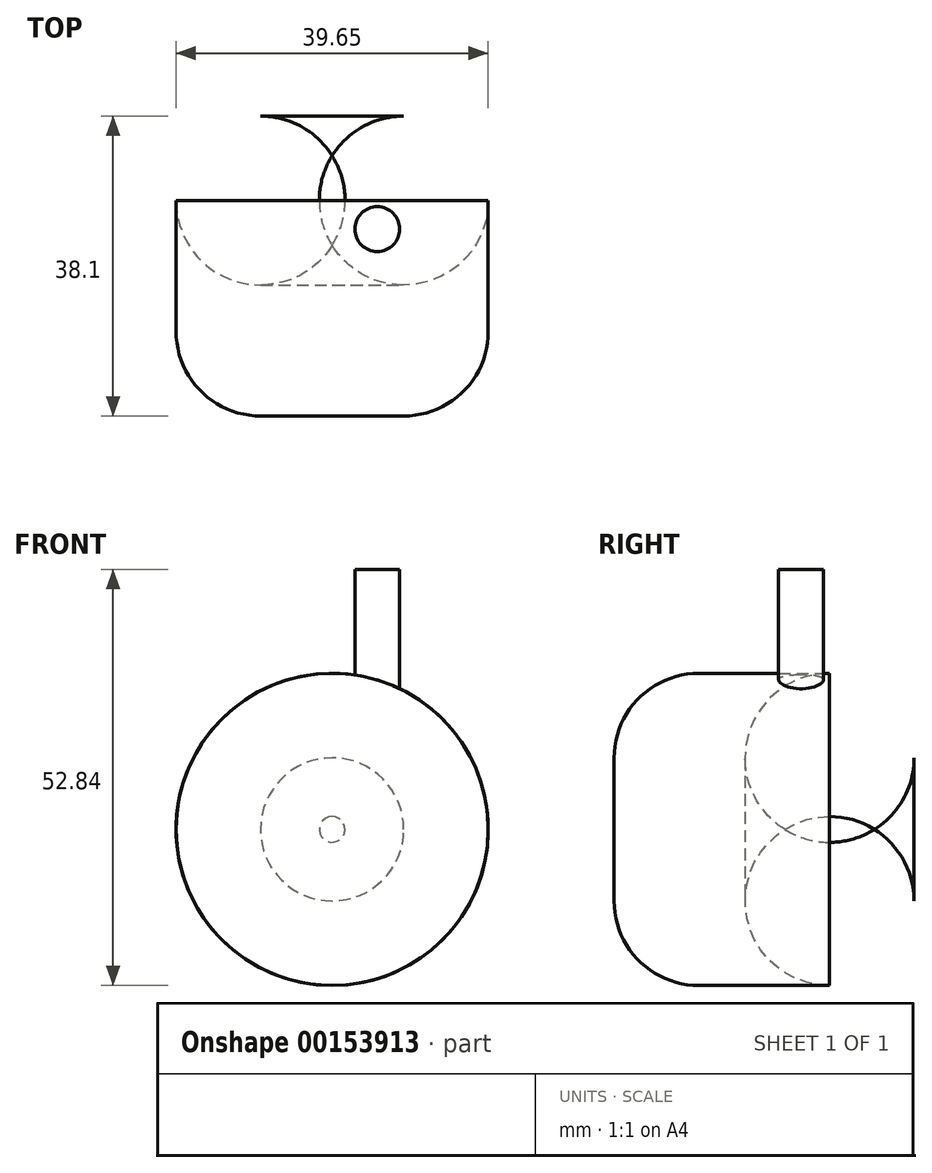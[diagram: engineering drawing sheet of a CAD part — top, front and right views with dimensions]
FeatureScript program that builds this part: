
annotation { "Feature Type Name" : "Feature", "Feature Type Description" : "" }
export const myFeature = defineFeature(function(context is Context, id is Id, definition is map)
    precondition{}
    {
        {
            var Q0;
            Q0=qCreatedBy(makeId("Front.planeOp"),FACE);
            var sketch = newSketch(context, id + "F0", { "sketchPlane" : qUnion([Q0])});
            skCircle(sketch, "E0", {"center": v(-19.47, 16.51) * mm, "radius": 19.82 * mm});
            skSolve(sketch);
        }
        {
            var Q0;
            Q0 = qSketchRegion(id + "F0", true);
            extrude(context, id + "F1", {"entities" : qUnion([Q0]), "depth" : 38.1 * mm});
        }
        {
            var Q0;
            Q0=makeQuery(id+"F1.opExtrude","CAP_EDGE",EDGE,{"disambiguationData":[OSD([sQuery(id+"F0.wireOp",EDGE,"E0")])],"isStart":false});
            var Q1;
            Q1=makeQuery(id+"F1.opExtrude","CAP_EDGE",EDGE,{"disambiguationData":[OSD([sQuery(id+"F0.wireOp",EDGE,"E0")])],"isStart":true});
            fillet(context, id + "F2", {"entities" : qUnion([Q0, Q1]), "radius" : 10.73 * mm, "tangentPropagation" : true, "allowEdgeOverflow" : false});
        }
        {
            var Q0;
            Q0=qCreatedBy(makeId("Top.planeOp"),FACE);
            var sketch = newSketch(context, id + "F3", { "sketchPlane" : qUnion([Q0])});
            skCircle(sketch, "E1", {"center": v(-13.74, -14.36) * mm, "radius": 2.84 * mm});
            skSolve(sketch);
        }
        {
            var Q0;
            Q0 = qSketchRegion(id + "F3", true);
            extrude(context, id + "F4", {"entities" : qUnion([Q0]), "operationType" : NewBodyOperationType.ADD, "depth" : 49.53 * mm});
        }
    });
